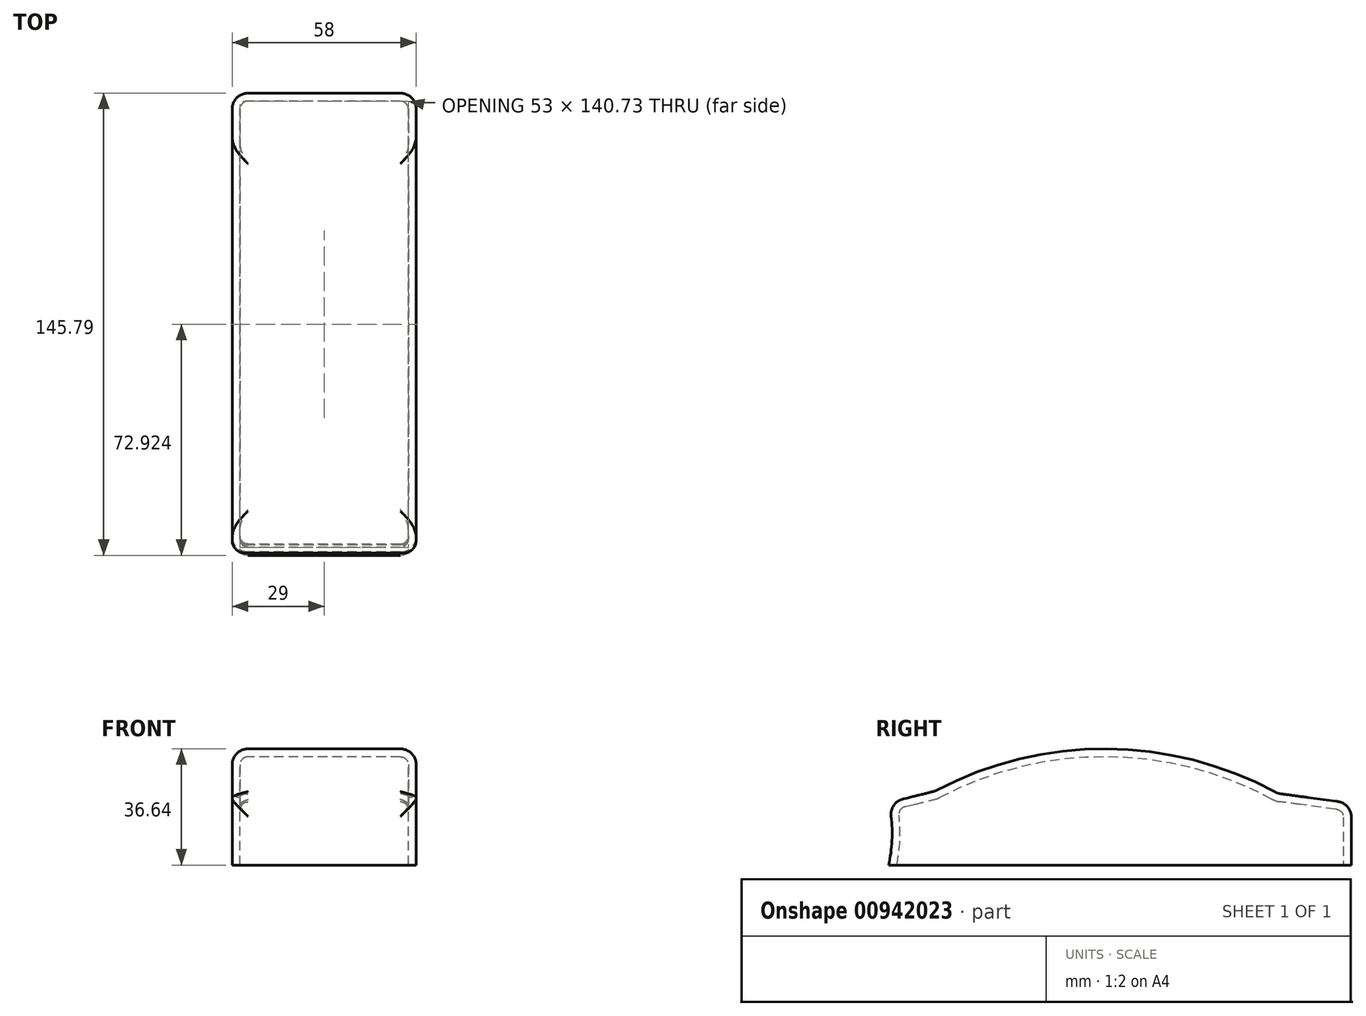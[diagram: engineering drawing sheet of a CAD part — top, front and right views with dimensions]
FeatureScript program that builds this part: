
annotation { "Feature Type Name" : "Feature", "Feature Type Description" : "" }
export const myFeature = defineFeature(function(context is Context, id is Id, definition is map)
    precondition{}
    {
        {
            var Q0;
            Q0=qCreatedBy(makeId("Right.planeOp"),FACE);
            var sketch = newSketch(context, id + "F0", { "sketchPlane" : qUnion([Q0])});
            skLineSegment(sketch, "E0", {"start": v(-71.58, 0) * mm, "end": v(74.2, 0) * mm});
            skLineSegment(sketch, "E1", {"start": v(74.2, 0) * mm, "end": v(74.2, 19.48) * mm});
            skLineSegment(sketch, "E2", {"start": v(74.2, 19.48) * mm, "end": v(51.03, 22.58) * mm});
            skArc(sketch, "E3", {"start": v(-71.58, 0) * mm, "mid": v(-70.49, 9.86) * mm, "end": v(-71.58, 19.72) * mm});
            skLineSegment(sketch, "E4", {"start": v(-71.58, 19.72) * mm, "end": v(-57, 23.3) * mm});
            skArc(sketch, "E5", {"start": v(51.03, 22.58) * mm, "mid": v(-2.9, 36.64) * mm, "end": v(-57, 23.3) * mm});
            skPoint(sketch, "E6.center.orphan", {"position": v(-43.14, 2) * mm});
            skPoint(sketch, "E7.center.orphan", {"position": v(28.08, 2) * mm});
            skArc(sketch, "E8", {"start": v(39.91, 0) * mm, "mid": v(28.08, 14) * mm, "end": v(16.25, 0) * mm});
            skArc(sketch, "E9", {"start": v(-31.3, 0) * mm, "mid": v(-43.14, 14) * mm, "end": v(-54.97, 0) * mm});
            skSolve(sketch);
        }
        {
            var Q0;
            Q0 = qSketchRegion(id + "F0", true);
            extrude(context, id + "F1", {"entities" : qUnion([Q0]), "endBound" : BoundingType.SYMMETRIC, "depth" : 58 * mm, "offsetDistance" : 25 * mm});
        }
        {
            var Q0;
            Q0=makeQuery(id+"F1.opExtrude","SWEPT_EDGE",EDGE,{"disambiguationData":[OSD([sQuery(id+"F0.wireOp",EDGE,"E3"),sQuery(id+"F0.wireOp",EDGE,"E4")])]});
            var Q1;
            Q1=makeQuery(id+"F1.opExtrude","CAP_EDGE",EDGE,{"disambiguationData":[OSD([sQuery(id+"F0.wireOp",EDGE,"E3")])],"isStart":true});
            var Q2;
            Q2=makeQuery(id+"F1.opExtrude","SWEPT_EDGE",EDGE,{"disambiguationData":[OSD([sQuery(id+"F0.wireOp",EDGE,"E4"),sQuery(id+"F0.wireOp",EDGE,"E5")])]});
            var Q3;
            Q3=makeQuery(id+"F1.opExtrude","CAP_EDGE",EDGE,{"disambiguationData":[OSD([sQuery(id+"F0.wireOp",EDGE,"E3")])],"isStart":false});
            var Q4;
            Q4=makeQuery(id+"F1.opExtrude","CAP_EDGE",EDGE,{"disambiguationData":[OSD([sQuery(id+"F0.wireOp",EDGE,"E5")])],"isStart":true});
            var Q5;
            Q5=makeQuery(id+"F1.opExtrude","SWEPT_FACE",FACE,{"disambiguationData":[OSD([sQuery(id+"F0.wireOp",EDGE,"E5")])]});
            var Q6;
            Q6=makeQuery(id+"F1.opExtrude","SWEPT_EDGE",EDGE,{"disambiguationData":[OSD([sQuery(id+"F0.wireOp",EDGE,"E1"),sQuery(id+"F0.wireOp",EDGE,"E2")])]});
            var Q7;
            Q7=makeQuery(id+"F1.opExtrude","CAP_EDGE",EDGE,{"disambiguationData":[OSD([sQuery(id+"F0.wireOp",EDGE,"E1")])],"isStart":false});
            var Q8;
            Q8=makeQuery(id+"F1.opExtrude","CAP_EDGE",EDGE,{"disambiguationData":[OSD([sQuery(id+"F0.wireOp",EDGE,"E1")])],"isStart":true});
            fillet(context, id + "F2", {"entities" : qUnion([Q0, Q1, Q2, Q3, Q4, Q5, Q6, Q7, Q8]), "radius" : 5 * mm, "tangentPropagation" : true, "allowEdgeOverflow" : false});
        }
        {
            var Q0;
            Q0=makeQuery(id+"F1.opExtrude","SWEPT_FACE",FACE,{"disambiguationData":[OSD([sQuery(id+"F0.wireOp",EDGE,"E0")])]});
            shell(context, id + "F3", {"entities" : qUnion([Q0]), "thickness" : 2.5 * mm});
        }
    });
